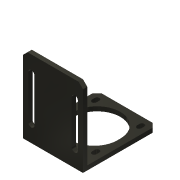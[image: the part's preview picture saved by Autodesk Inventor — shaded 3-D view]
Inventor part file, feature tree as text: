
AUTODESK INVENTOR PART (.ipt)
format: ipt  version: 2014 (Build 180170000, 170)  size: 151,040 bytes
history: native  units: mm
features: extrude x2, sketch x2, chamfer x1
ambient origin geometry x8: Origin, YZ Plane, XZ Plane, XY Plane, X Axis, Y Axis, Z Axis, Center Point
bodies: Solid1 (feature_tree)
feature tree (5):
  extrude  "Extrusion1"  Depth=41.3mm
  extrude  "Extrusion3"  Depth=3.0mm
  chamfer  "Chamfer1"  Distance=16.0mm
  sketch  "Sketch1"  dims[d0=51.0mm d1=41.3mm]
  sketch  "Sketch2"  dims[d2=28.4mm d3=2.0mm d4=16.0mm d5=2.0mm d6=31.0mm d7=31.0mm d8=1.6mm d10=15.5mm d11=15.5mm d12=3.0mm d13=0.0mm d14=53.0mm d19=3.0mm d20=2.0mm d21=45.0deg d22=51.0mm d23=4.3mm d24=30.0mm d25=30.0mm d26=3.0mm d27=0.0mm]
